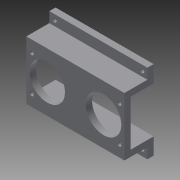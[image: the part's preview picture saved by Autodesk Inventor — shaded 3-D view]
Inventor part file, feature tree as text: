
AUTODESK INVENTOR PART (.ipt)
format: ipt  version: 2015 (Build 190159000, 159)  size: 179,200 bytes
history: native  units: in
note: dims shown in document units (in); Inventor stores cm internally (conversion verified against a paired STEP export)
features: reference x16, extrude x8, sketch x8
ambient origin geometry x8: Origin, YZ Plane, XZ Plane, XY Plane, X Axis, Y Axis, Z Axis, Center Point
bodies: Solid1 (feature_tree)
feature tree (32):
  extrude  "Extrusion1"  Depth=1.8504in
  extrude  "Extrusion2"  Depth=0.0394in
  extrude  "Extrusion3"  Depth=0.0394in
  extrude  "Extrusion4"  Depth=0.1181in
  extrude  "Extrusion5"  Depth=0.8661in
  extrude  "Extrusion6"  Depth=0.1969in
  extrude  "Extrusion7"  Depth=0.1969in
  extrude  "Extrusion8"  Depth=0.1181in TaperAngle=0.0deg
  sketch  "Sketch1"  dims[d0=0.6693in d1=1.8504in]
  reference  "Reference1"
  reference  "Reference2"
  reference  "Reference3"
  reference  "Reference4"
  reference  "Reference5"
  reference  "Reference6"
  reference  "Reference7"
  reference  "Reference8"
  reference  "Reference9"
  reference  "Reference10"
  reference  "Reference11"
  reference  "Reference12"
  sketch  "Sketch5"  dims[d2=0.8661in d3=0.0394in]
  sketch  "Sketch6"  dims[d4=0.0394in d5=0.6693in]
  reference  "Reference14"
  reference  "Reference15"
  reference  "Reference16"
  reference  "Reference17"
  sketch  "Sketch8"  dims[d6=0.1181in d7=0.0in d12=0.1181in]
  sketch  "Sketch9"  dims[d14=0.1181in d15=0.8661in]
  sketch  "Sketch10"  dims[d16=1.8504in d17=0.0in d18=0.1969in]
  sketch  "Sketch11"  dims[d19=0.1969in d20=0.1969in]
  sketch  "Sketch12"  dims[d21=1.8504in d22=0.0in d23=0.1181in d24=0.0in d25=0.1181in d26=0.0in d27=0.1181in d28=0.1969in d29=0.0in d30=0.1181in d31=0.1969in d32=0.0in d36=0.079in d37=0.079in d38=0.098in d39=0.1969in d40=0.0in]
